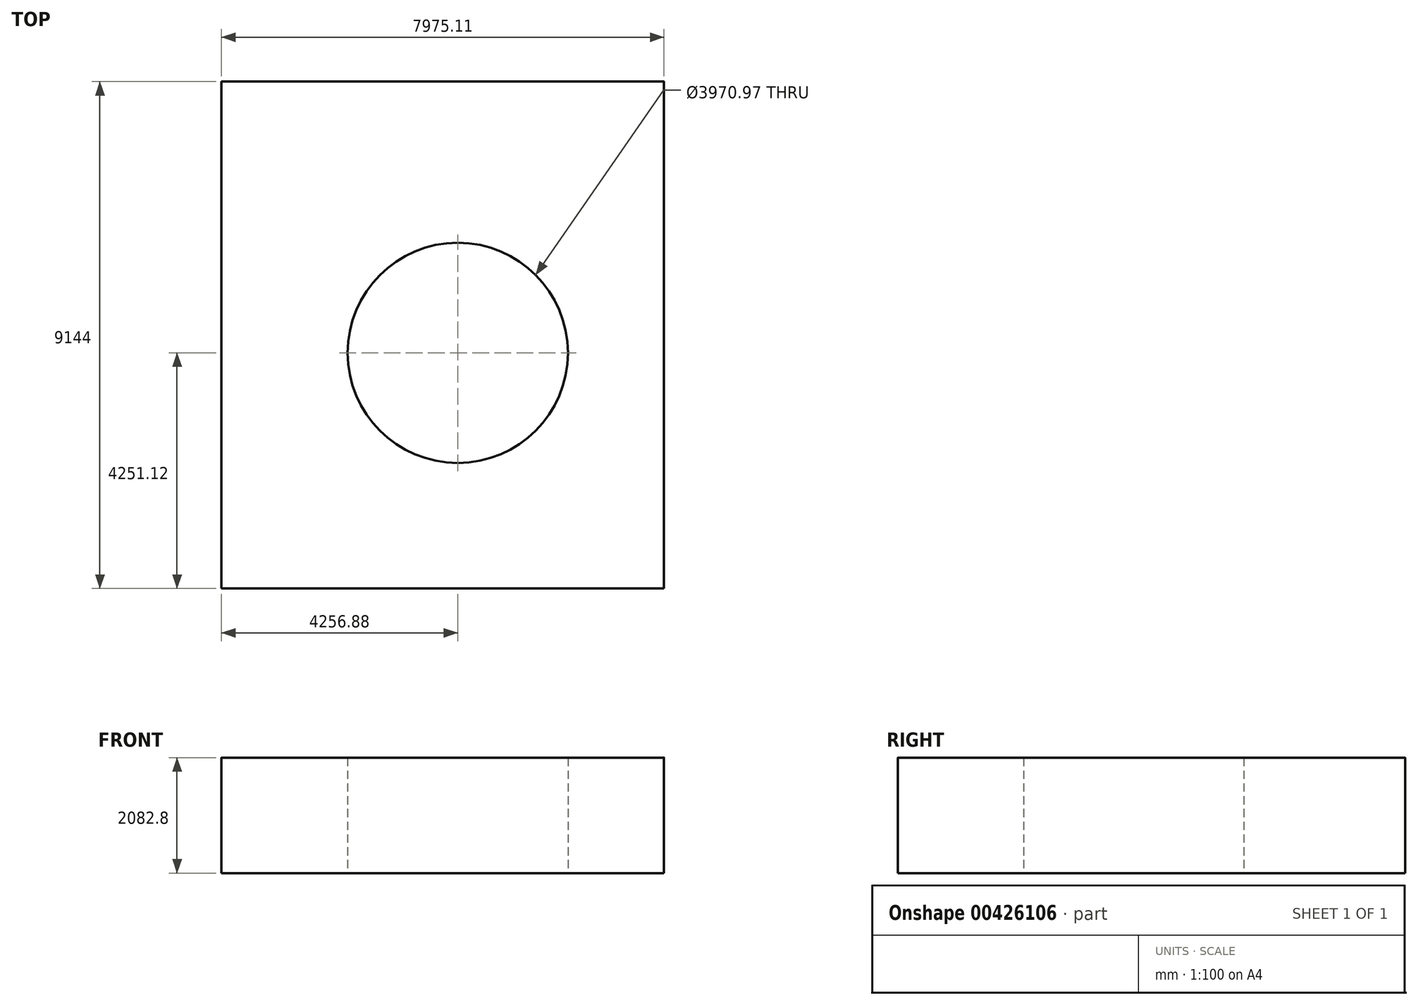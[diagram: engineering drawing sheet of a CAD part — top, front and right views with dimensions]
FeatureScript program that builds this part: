
annotation { "Feature Type Name" : "Feature", "Feature Type Description" : "" }
export const myFeature = defineFeature(function(context is Context, id is Id, definition is map)
    precondition{}
    {
        {
            var Q0;
            Q0=qCreatedBy(makeId("Top.planeOp"),FACE);
            var sketch = newSketch(context, id + "F0", { "sketchPlane" : qUnion([Q0])});
            skLineSegment(sketch, "E0.bottom", {"start": v(-4256.88, -4251.12) * mm, "end": v(3718.23, -4251.12) * mm});
            skLineSegment(sketch, "E0.top", {"start": v(-4256.88, 4892.88) * mm, "end": v(3718.23, 4892.88) * mm});
            skLineSegment(sketch, "E0.left", {"start": v(-4256.88, -4251.12) * mm, "end": v(-4256.88, 4892.88) * mm});
            skLineSegment(sketch, "E0.right", {"start": v(3718.23, -4251.12) * mm, "end": v(3718.23, 4892.88) * mm});
            skCircle(sketch, "E1", {"center": v(0, 0) * mm, "radius": 1985.48 * mm});
            skSolve(sketch);
        }
        {
            var Q0;
            Q0=makeQuery(id+"F0.imprint","IMPRINT",FACE,{"disambiguationData":[TD([[makeQuery(id+"F0.imprint","IMPRINT",EDGE,{"derivedFrom":sQuery(id+"F0.wireOp",EDGE,"E0.bottom")}),1.0]])]});
            extrude(context, id + "F1", {"entities" : qUnion([Q0]), "depth" : 2082.8 * mm});
        }
        {
            var Q0;
            Q0=makeQuery(id+"F1.opExtrude","CAP_FACE",FACE,{"disambiguationData":[OSD([sQuery(id+"F0.wireOp",EDGE,"E0.bottom"),sQuery(id+"F0.wireOp",EDGE,"E0.top"),sQuery(id+"F0.wireOp",EDGE,"E0.left"),sQuery(id+"F0.wireOp",EDGE,"E0.right"),sQuery(id+"F0.wireOp",EDGE,"E1")])],"isStart":false});
            fillet(context, id + "F2", {"entities" : qUnion([Q0]), "radius" : 5.08 * mm, "tangentPropagation" : true, "allowEdgeOverflow" : false});
        }
    });
